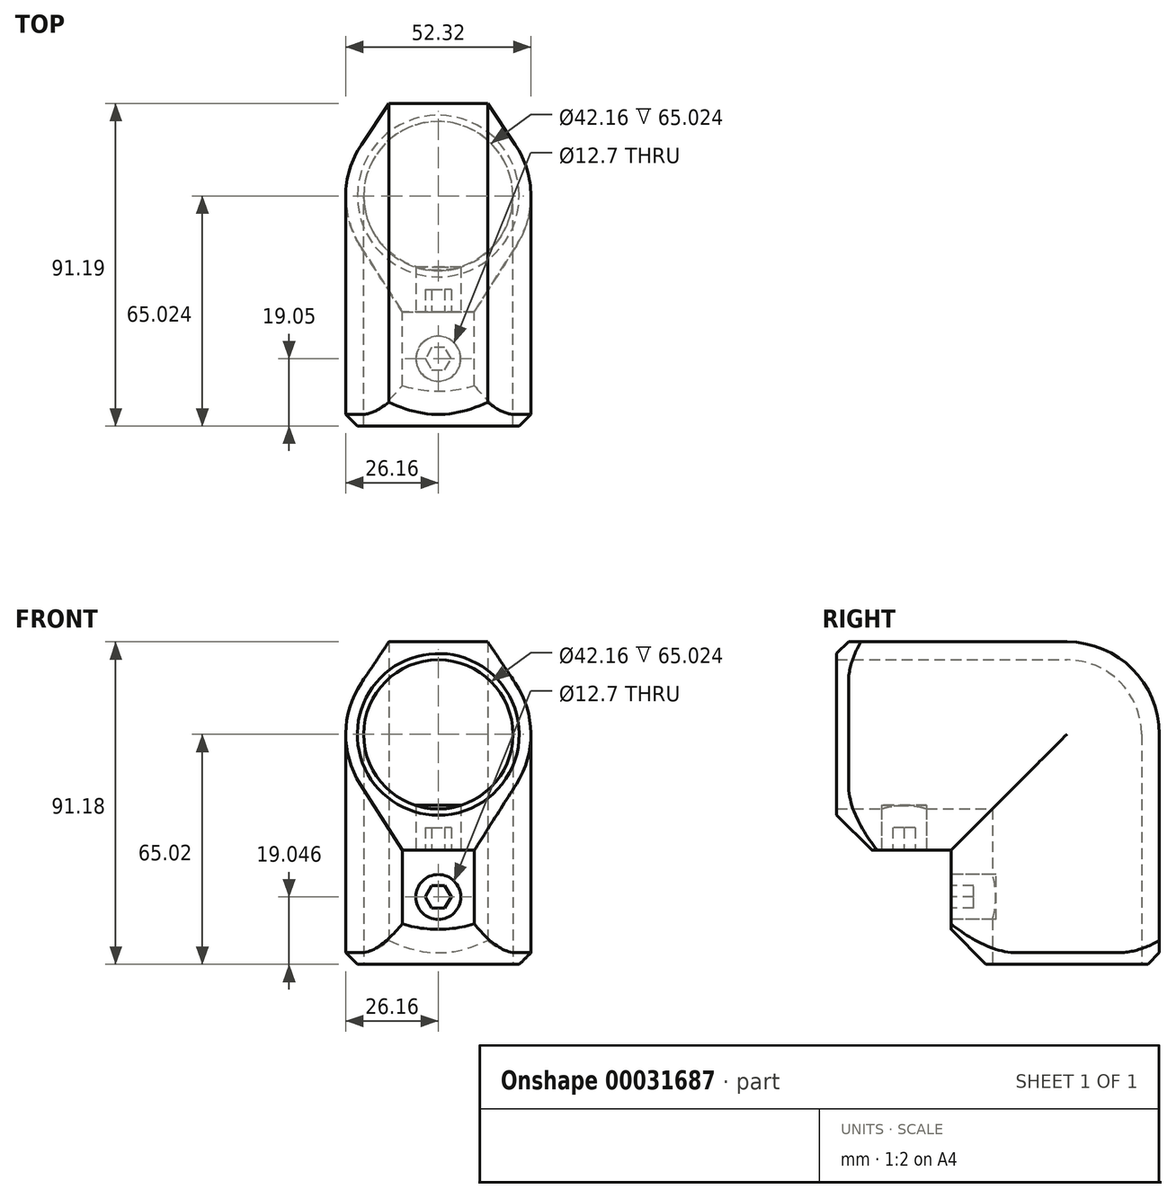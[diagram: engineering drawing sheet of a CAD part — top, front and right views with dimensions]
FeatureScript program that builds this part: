
annotation { "Feature Type Name" : "Feature", "Feature Type Description" : "" }
export const myFeature = defineFeature(function(context is Context, id is Id, definition is map)
    precondition{}
    {
        {
            var Q0;
            Q0=qCreatedBy(makeId("Front.planeOp"),FACE);
            var sketch = newSketch(context, id + "F0", { "sketchPlane" : qUnion([Q0])});
            skCircle(sketch, "E0", {"center": v(0, 0) * mm, "radius": 21.08 * mm});
            skCircle(sketch, "E1", {"center": v(0, 0) * mm, "radius": 26.16 * mm});
            skLineSegment(sketch, "E2", {"start": v(0, 26.16) * mm, "end": v(-13.97, 26.16) * mm});
            skLineSegment(sketch, "E3", {"start": v(-13.97, 26.16) * mm, "end": v(-21.74, 14.55) * mm});
            skLineSegment(sketch, "E4", {"start": v(0, -32.77) * mm, "end": v(-10.16, -32.77) * mm});
            skLineSegment(sketch, "E5", {"start": v(-10.16, -32.77) * mm, "end": v(-22.07, -14.04) * mm});
            skLineSegment(sketch, "E6.MirrorCS", {"start": v(0, 26.16) * mm, "end": v(13.97, 26.16) * mm});
            skLineSegment(sketch, "E7.MirrorCS", {"start": v(13.97, 26.16) * mm, "end": v(21.74, 14.55) * mm});
            skLineSegment(sketch, "E8.MirrorCS", {"start": v(0, -32.77) * mm, "end": v(10.16, -32.77) * mm});
            skLineSegment(sketch, "E9.MirrorCS", {"start": v(10.16, -32.77) * mm, "end": v(22.07, -14.04) * mm});
            skLineSegment(sketch, "E10", {"start": v(-26.16, 0) * mm, "end": v(26.16, 0) * mm});
            skSolve(sketch);
        }
        {
            var Q0;
            Q0=qCreatedBy(makeId("Right.planeOp"),FACE);
            var sketch = newSketch(context, id + "F1", { "sketchPlane" : qUnion([Q0])});
            skLineSegment(sketch, "E11", {"start": v(0, 0) * mm, "end": v(65.02, 0) * mm});
            skLineSegment(sketch, "E12", {"start": v(65.02, 0) * mm, "end": v(65.02, -65.02) * mm});
            skLineSegment(sketch, "E13", {"start": v(0, 26.16) * mm, "end": v(65.02, 26.16) * mm});
            skLineSegment(sketch, "E14", {"start": v(91.19, 0) * mm, "end": v(91.19, -65.02) * mm});
            skArc(sketch, "E15", {"start": v(65.02, 26.16) * mm, "mid": v(83.52, 18.5) * mm, "end": v(91.19, 0) * mm});
            skLineSegment(sketch, "E16", {"start": v(-38.24, 44.65) * mm, "end": v(-38.24, 0) * mm});
            skLineSegment(sketch, "E17", {"start": v(21.8, 44.65) * mm, "end": v(-38.24, 44.65) * mm});
            skLineSegment(sketch, "E18", {"start": v(-22.86, 0) * mm, "end": v(21.8, 44.65) * mm});
            skLineSegment(sketch, "E19", {"start": v(65.02, -87.88) * mm, "end": v(111.83, -41.08) * mm});
            skLineSegment(sketch, "E20", {"start": v(111.83, -41.08) * mm, "end": v(111.83, -120.7) * mm});
            skLineSegment(sketch, "E21", {"start": v(111.83, -120.7) * mm, "end": v(65.02, -120.7) * mm});
            skLineSegment(sketch, "E22", {"start": v(-38.24, 0) * mm, "end": v(-22.86, 0) * mm});
            skLineSegment(sketch, "E23", {"start": v(65.02, -120.7) * mm, "end": v(65.02, -87.88) * mm});
            skSolve(sketch);
        }
        {
            var Q0;
            {var subQ0=sQuery(id+"F0.wireOp",EDGE,"E10");var subQ1=sQuery(id+"F0.wireOp",EDGE,"E0");var subQ5=makeQuery(id+"F0.imprint","INTERSECT",VERTEX,{"disambiguationData":[OD(0.0)],"derivedFrom":[subQ1,subQ0]});Q0=makeQuery(id+"F0.imprint","IMPRINT",FACE,{"disambiguationData":[TD([[makeQuery(id+"F0.imprint","IMPRINT",EDGE,{"disambiguationData":[TD([[subQ5,1.0]])],"derivedFrom":subQ1}),-1.0]])]});}
            var Q1;
            Q1=makeQuery(id+"F0.imprint","IMPRINT",FACE,{"disambiguationData":[TD([[makeQuery(id+"F0.imprint","IMPRINT",EDGE,{"derivedFrom":sQuery(id+"F0.wireOp",EDGE,"E2")}),1.0]])]});
            var Q2;
            {var subQ1=sQuery(id+"F0.wireOp",EDGE,"E6.MirrorCS");Q2=makeQuery(id+"F0.imprint","IMPRINT",FACE,{"disambiguationData":[TD([[makeQuery(id+"F0.imprint","IMPRINT",EDGE,{"derivedFrom":subQ1}),-1.0]])]});}
            var Q3;
            Q3=sQuery(id+"F1.wireOp",EDGE,"E13");
            var Q4;
            Q4=sQuery(id+"F1.wireOp",EDGE,"E15");
            var Q5;
            Q5=sQuery(id+"F1.wireOp",EDGE,"E14");
            sweep(context, id + "F2", {"profiles" : qUnion([Q0, Q1, Q2]), "path" : qUnion([Q3, Q4, Q5])});
        }
        {
            var Q0;
            {var subQ0=sQuery(id+"F0.wireOp",EDGE,"E10");var subQ1=sQuery(id+"F0.wireOp",EDGE,"E0");var subQ5=makeQuery(id+"F0.imprint","INTERSECT",VERTEX,{"disambiguationData":[OD(0.0)],"derivedFrom":[subQ1,subQ0]});Q0=makeQuery(id+"F0.imprint","IMPRINT",FACE,{"disambiguationData":[TD([[makeQuery(id+"F0.imprint","IMPRINT",EDGE,{"disambiguationData":[TD([[subQ5,-1.0]])],"derivedFrom":subQ1}),-1.0]])]});}
            var Q1;
            Q1=makeQuery(id+"F0.imprint","IMPRINT",FACE,{"disambiguationData":[TD([[makeQuery(id+"F0.imprint","IMPRINT",EDGE,{"derivedFrom":sQuery(id+"F0.wireOp",EDGE,"E4")}),-1.0]])]});
            var Q2;
            Q2=sQuery(id+"F1.wireOp",EDGE,"E11");
            var Q3;
            Q3=sQuery(id+"F1.wireOp",EDGE,"E12");
            sweep(context, id + "F3", {"operationType" : NewBodyOperationType.ADD, "profiles" : qUnion([Q0, Q1]), "path" : qUnion([Q2, Q3])});
        }
        {
            var Q0;
            Q0=makeQuery(id+"F1.imprint","IMPRINT",FACE,{"disambiguationData":[TD([[makeQuery(id+"F1.imprint","IMPRINT",EDGE,{"derivedFrom":sQuery(id+"F1.wireOp",EDGE,"E16")}),1.0]])]});
            var Q1;
            Q1=sQuery(id+"F1.wireOp",EDGE,"E22");
            revolve(context, id + "F4", {"operationType" : NewBodyOperationType.REMOVE, "entities" : qUnion([Q0]), "axis" : qUnion([Q1]), "revolveType" : RevolveType.FULL, "oppositeDirection" : true});
        }
        {
            var Q0;
            {var subQ1=sQuery(id+"F1.wireOp",EDGE,"E20");Q0=makeQuery(id+"F1.imprint","IMPRINT",FACE,{"disambiguationData":[TD([[makeQuery(id+"F1.imprint","IMPRINT",EDGE,{"derivedFrom":subQ1}),-1.0]])]});}
            var Q1;
            Q1=sQuery(id+"F1.wireOp",EDGE,"E23");
            revolve(context, id + "F5", {"operationType" : NewBodyOperationType.REMOVE, "entities" : qUnion([Q0]), "axis" : qUnion([Q1]), "revolveType" : RevolveType.FULL, "oppositeDirection" : true});
        }
        {
            var Q0;
            Q0=makeQuery(id+"F3.opSweep","SWEPT_FACE",FACE,{"disambiguationData":[OSD([sQuery(id+"F0.wireOp",EDGE,"E4"),sQuery(id+"F0.wireOp",EDGE,"E8.MirrorCS"),sQuery(id+"F1.wireOp",EDGE,"E11")])]});
            var sketch = newSketch(context, id + "F6", { "sketchPlane" : qUnion([Q0])});
            skCircle(sketch, "E24", {"center": v(0, -19.05) * mm, "radius": 6.35 * mm});
            skCircle(sketch, "E25.cCircle", {"center": v(0, -19.05) * mm, "radius": 3.18 * mm, "construction": true});
            skLineSegment(sketch, "E25.0", {"start": v(-1.83, -15.88) * mm, "end": v(1.83, -15.88) * mm});
            skLineSegment(sketch, "E25.1", {"start": v(1.83, -15.88) * mm, "end": v(3.67, -19.05) * mm});
            skLineSegment(sketch, "E25.2", {"start": v(3.67, -19.05) * mm, "end": v(1.83, -22.23) * mm});
            skLineSegment(sketch, "E25.3", {"start": v(1.83, -22.23) * mm, "end": v(-1.83, -22.23) * mm});
            skLineSegment(sketch, "E25.4", {"start": v(-1.83, -22.23) * mm, "end": v(-3.67, -19.05) * mm});
            skLineSegment(sketch, "E25.5", {"start": v(-3.67, -19.05) * mm, "end": v(-1.83, -15.88) * mm});
            skPoint(sketch, "E25.0.midPoint", {"position": v(0, -15.88) * mm});
            skSolve(sketch);
        }
        {
            var Q0;
            Q0=makeQuery(id+"F3.opSweep","SWEPT_FACE",FACE,{"disambiguationData":[OSD([sQuery(id+"F0.wireOp",EDGE,"E4"),sQuery(id+"F0.wireOp",EDGE,"E8.MirrorCS"),sQuery(id+"F1.wireOp",EDGE,"E12")])]});
            var sketch = newSketch(context, id + "F7", { "sketchPlane" : qUnion([Q0])});
            skCircle(sketch, "E26", {"center": v(0, -45.97) * mm, "radius": 6.35 * mm});
            skCircle(sketch, "E27.cCircle", {"center": v(0, -45.97) * mm, "radius": 3.17 * mm, "construction": true});
            skLineSegment(sketch, "E27.0", {"start": v(-1.83, -42.8) * mm, "end": v(1.83, -42.8) * mm});
            skLineSegment(sketch, "E27.1", {"start": v(1.83, -42.8) * mm, "end": v(3.67, -45.97) * mm});
            skLineSegment(sketch, "E27.2", {"start": v(3.67, -45.97) * mm, "end": v(1.83, -49.15) * mm});
            skLineSegment(sketch, "E27.3", {"start": v(1.83, -49.15) * mm, "end": v(-1.83, -49.15) * mm});
            skLineSegment(sketch, "E27.4", {"start": v(-1.83, -49.15) * mm, "end": v(-3.67, -45.97) * mm});
            skLineSegment(sketch, "E27.5", {"start": v(-3.67, -45.97) * mm, "end": v(-1.83, -42.8) * mm});
            skPoint(sketch, "E27.0.midPoint", {"position": v(0, -42.8) * mm});
            skSolve(sketch);
        }
        {
            var Q0;
            Q0=makeQuery(id+"F6.imprint","IMPRINT",FACE,{"disambiguationData":[TD([[makeQuery(id+"F6.imprint","IMPRINT",EDGE,{"derivedFrom":sQuery(id+"F6.wireOp",EDGE,"E24")}),1.0]])]});
            var Q1;
            Q1=makeQuery(id+"F6.imprint","IMPRINT",FACE,{"disambiguationData":[TD([[makeQuery(id+"F6.imprint","IMPRINT",EDGE,{"derivedFrom":sQuery(id+"F6.wireOp",EDGE,"E25.0")}),-1.0]])]});
            extrude(context, id + "F8", {"entities" : qUnion([Q0, Q1]), "oppositeDirection" : true, "depth" : 12.7 * mm});
        }
        {
            var Q0;
            Q0=makeQuery(id+"F7.imprint","IMPRINT",FACE,{"disambiguationData":[TD([[makeQuery(id+"F7.imprint","IMPRINT",EDGE,{"derivedFrom":sQuery(id+"F7.wireOp",EDGE,"E27.0")}),-1.0]])]});
            var Q1;
            Q1=makeQuery(id+"F7.imprint","IMPRINT",FACE,{"disambiguationData":[TD([[makeQuery(id+"F7.imprint","IMPRINT",EDGE,{"derivedFrom":sQuery(id+"F7.wireOp",EDGE,"E26")}),1.0]])]});
            extrude(context, id + "F9", {"entities" : qUnion([Q0, Q1]), "oppositeDirection" : true, "depth" : 12.7 * mm});
        }
        {
            var Q0;
            Q0=makeQuery(id+"F8.opExtrude","SWEPT_BODY",BODY,{"disambiguationData":[OSD([sQuery(id+"F6.wireOp",EDGE,"E24")])]});
            var Q1;
            Q1=makeQuery(id+"F9.opExtrude","SWEPT_BODY",BODY,{"disambiguationData":[OSD([sQuery(id+"F7.wireOp",EDGE,"E26")])]});
            var Q2;
            Q2=makeQuery(id+"F2.opSweep","SWEPT_BODY",BODY,{"disambiguationData":[OSD([sQuery(id+"F0.wireOp",EDGE,"E0"),sQuery(id+"F0.wireOp",EDGE,"E1"),sQuery(id+"F0.wireOp",EDGE,"E2"),sQuery(id+"F0.wireOp",EDGE,"E3"),sQuery(id+"F0.wireOp",EDGE,"E6.MirrorCS"),sQuery(id+"F0.wireOp",EDGE,"E7.MirrorCS"),sQuery(id+"F0.wireOp",EDGE,"E10"),sQuery(id+"F1.wireOp",EDGE,"E14")])]});
            booleanBodies(context, id + "F10", {"operationType" : BooleanOperationType.SUBTRACTION, "tools" : qUnion([Q0, Q1]), "targets" : qUnion([Q2]), "keepTools" : true});
        }
        {
            var Q0;
            Q0=makeQuery(id+"F7.imprint","IMPRINT",FACE,{"disambiguationData":[TD([[makeQuery(id+"F7.imprint","IMPRINT",EDGE,{"derivedFrom":sQuery(id+"F7.wireOp",EDGE,"E27.0")}),-1.0]])]});
            extrude(context, id + "F11", {"entities" : qUnion([Q0]), "operationType" : NewBodyOperationType.REMOVE, "oppositeDirection" : true, "depth" : 6.35 * mm});
        }
        {
            var Q0;
            Q0=makeQuery(id+"F6.imprint","IMPRINT",FACE,{"disambiguationData":[TD([[makeQuery(id+"F6.imprint","IMPRINT",EDGE,{"derivedFrom":sQuery(id+"F6.wireOp",EDGE,"E25.0")}),-1.0]])]});
            extrude(context, id + "F12", {"entities" : qUnion([Q0]), "operationType" : NewBodyOperationType.REMOVE, "oppositeDirection" : true, "depth" : 6.35 * mm});
        }
    });
